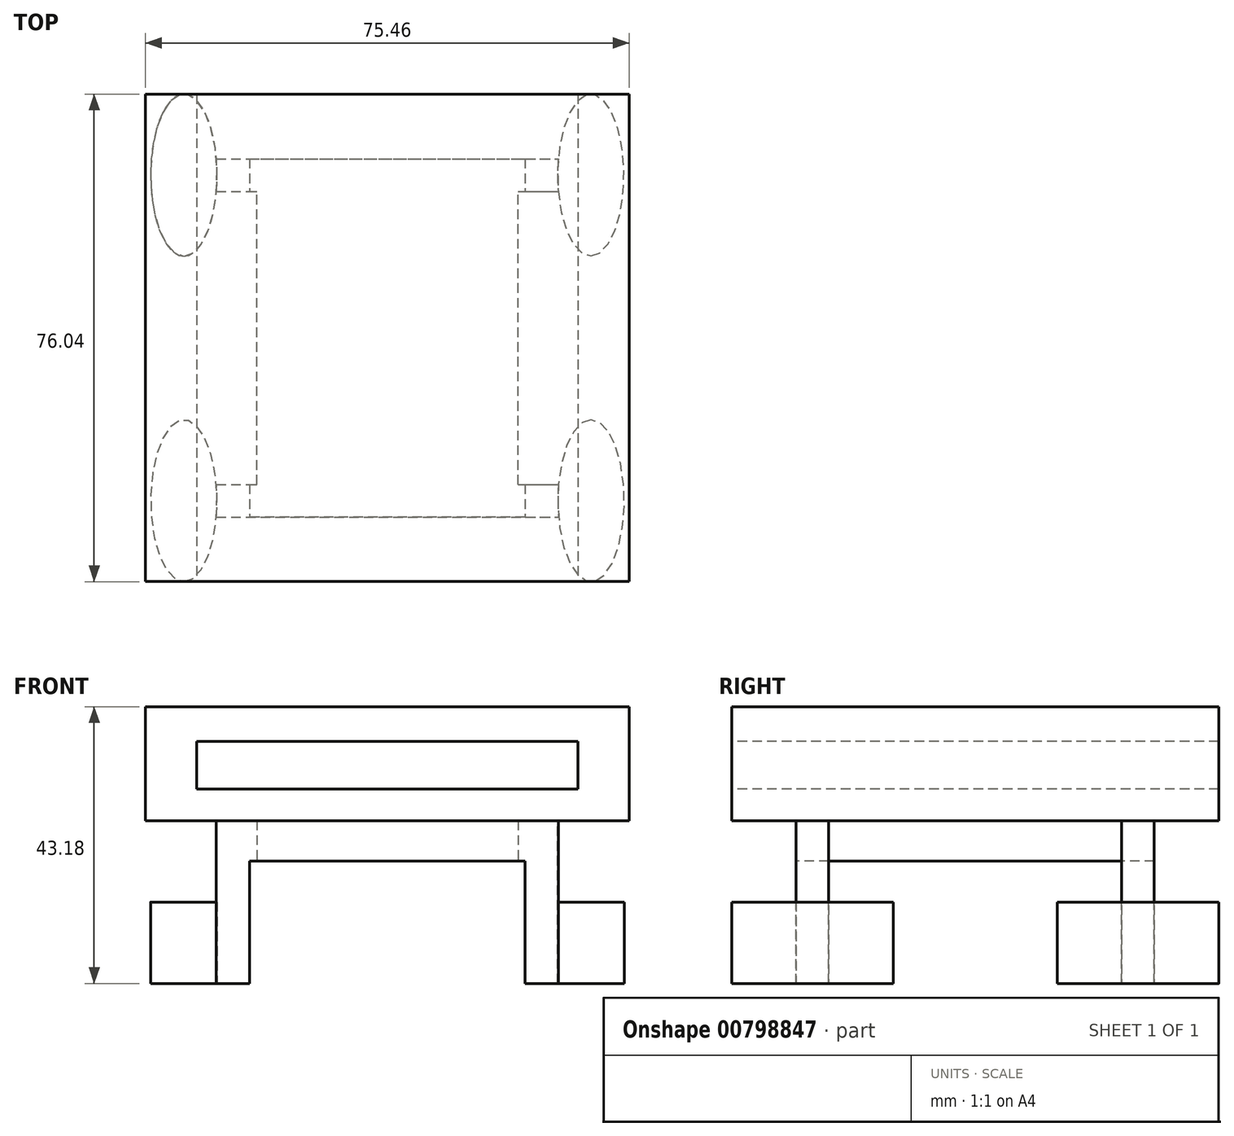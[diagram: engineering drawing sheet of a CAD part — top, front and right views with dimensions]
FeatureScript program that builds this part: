
annotation { "Feature Type Name" : "Feature", "Feature Type Description" : "" }
export const myFeature = defineFeature(function(context is Context, id is Id, definition is map)
    precondition{}
    {
        {
            var Q0;
            Q0=qCreatedBy(makeId("Top.planeOp"),FACE);
            var sketch = newSketch(context, id + "F0", { "sketchPlane" : qUnion([Q0])});
            skEllipse(sketch, "E0", {"center": v(-31.75, 25.4) * mm, "majorRadius": 12.62 * mm, "minorRadius": 5.19 * mm, "majorAxis": v(0, -1)});
            skEllipse(sketch, "E1.2.0", {"center": v(31.8, -25.4) * mm, "majorRadius": 12.62 * mm, "minorRadius": 5.19 * mm, "majorAxis": v(0, 1)});
            skPoint(sketch, "E1.center", {"position": v(0.02, 0) * mm});
            skEllipse(sketch, "E2", {"center": v(31.75, 25.4) * mm, "majorRadius": 12.6 * mm, "minorRadius": 5.18 * mm, "majorAxis": v(0, -1)});
            skEllipse(sketch, "E3", {"center": v(-31.75, -25.4) * mm, "majorRadius": 12.6 * mm, "minorRadius": 5.18 * mm, "majorAxis": v(0, -1)});
            skLineSegment(sketch, "E4", {"start": v(-26.67, 22.86) * mm, "end": v(-20.35, 22.86) * mm});
            skLineSegment(sketch, "E5.MirrorCS", {"start": v(-26.67, 27.94) * mm, "end": v(26.67, 27.94) * mm});
            skPoint(sketch, "E6.orphan", {"position": v(0, 0) * mm});
            skLineSegment(sketch, "E7.MirrorCS", {"start": v(-26.66, -22.86) * mm, "end": v(-20.35, -22.86) * mm});
            skLineSegment(sketch, "E8.MirrorCS", {"start": v(-26.67, -27.94) * mm, "end": v(26.67, -27.94) * mm});
            skPoint(sketch, "E9.start.orphan", {"position": v(-37.19, 0) * mm});
            skPoint(sketch, "E10.end.orphan", {"position": v(26.6, -25.4) * mm});
            skPoint(sketch, "E10.start.orphan", {"position": v(-26.57, -25.4) * mm});
            skLineSegment(sketch, "E11", {"start": v(26.68, -22.86) * mm, "end": v(26.71, -22.86) * mm});
            skLineSegment(sketch, "E12", {"start": v(26.67, -27.94) * mm, "end": v(26.71, -27.94) * mm});
            skLineSegment(sketch, "E13", {"start": v(-26.67, -27.94) * mm, "end": v(-26.67, -27.94) * mm});
            skLineSegment(sketch, "E14", {"start": v(-26.66, -22.86) * mm, "end": v(-26.67, -22.86) * mm});
            skLineSegment(sketch, "E15.left", {"start": v(20.4, -22.86) * mm, "end": v(20.4, 22.86) * mm});
            skLineSegment(sketch, "E15.right", {"start": v(-20.35, -22.86) * mm, "end": v(-20.35, 22.86) * mm});
            skLineSegment(sketch, "E16.trimOffspring", {"start": v(20.4, -22.86) * mm, "end": v(26.68, -22.86) * mm});
            skLineSegment(sketch, "E17.trimOffspring", {"start": v(20.4, 22.86) * mm, "end": v(26.67, 22.86) * mm});
            skSolve(sketch);
        }
        {
            var Q0;
            {var subQ0=sQuery(id+"F0.wireOp",EDGE,"E0");var subQ1=makeQuery(id+"F0.imprint","INTERSECT",VERTEX,{"derivedFrom":[subQ0,sQuery(id+"F0.wireOp",EDGE,"E4")]});Q0=makeQuery(id+"F0.imprint","IMPRINT",FACE,{"disambiguationData":[TD([[makeQuery(id+"F0.imprint","IMPRINT",EDGE,{"disambiguationData":[TD([[subQ1,-1.0]])],"derivedFrom":subQ0}),1.0]])]});}
            var Q1;
            {var subQ0=sQuery(id+"F0.wireOp",EDGE,"E1.2.0");var subQ1=makeQuery(id+"F0.imprint","INTERSECT",VERTEX,{"derivedFrom":[subQ0,sQuery(id+"F0.wireOp",EDGE,"E11")]});Q1=makeQuery(id+"F0.imprint","IMPRINT",FACE,{"disambiguationData":[TD([[makeQuery(id+"F0.imprint","IMPRINT",EDGE,{"disambiguationData":[TD([[subQ1,-1.0]])],"derivedFrom":subQ0}),1.0]])]});}
            var Q2;
            {var subQ0=sQuery(id+"F0.wireOp",EDGE,"E2");var subQ1=makeQuery(id+"F0.imprint","INTERSECT",VERTEX,{"derivedFrom":[subQ0,sQuery(id+"F0.wireOp",EDGE,"E5.MirrorCS")]});Q2=makeQuery(id+"F0.imprint","IMPRINT",FACE,{"disambiguationData":[TD([[makeQuery(id+"F0.imprint","IMPRINT",EDGE,{"disambiguationData":[TD([[subQ1,-1.0]])],"derivedFrom":subQ0}),1.0]])]});}
            var Q3;
            {var subQ0=sQuery(id+"F0.wireOp",EDGE,"E3");var subQ1=makeQuery(id+"F0.imprint","INTERSECT",VERTEX,{"derivedFrom":[subQ0,sQuery(id+"F0.wireOp",EDGE,"E13")]});Q3=makeQuery(id+"F0.imprint","IMPRINT",FACE,{"disambiguationData":[TD([[makeQuery(id+"F0.imprint","IMPRINT",EDGE,{"disambiguationData":[TD([[subQ1,-1.0]])],"derivedFrom":subQ0}),1.0]])]});}
            extrude(context, id + "F1", {"entities" : qUnion([Q0, Q1, Q2, Q3]), "depth" : 12.7 * mm, "offsetDistance" : 25.4 * mm});
        }
        {
            var Q0;
            {var subQ3=sQuery(id+"F0.wireOp",EDGE,"E4");Q0=makeQuery(id+"F0.imprint","IMPRINT",FACE,{"disambiguationData":[TD([[makeQuery(id+"F0.imprint","IMPRINT",EDGE,{"derivedFrom":subQ3}),1.0]])]});}
            extrude(context, id + "F2", {"entities" : qUnion([Q0]), "depth" : 25.4 * mm, "offsetDistance" : 25.4 * mm});
        }
        {
            var Q0;
            Q0=makeQuery(id+"F2.opExtrude","CAP_FACE",FACE,{"disambiguationData":[OSD([sQuery(id+"F0.wireOp",EDGE,"E0"),sQuery(id+"F0.wireOp",EDGE,"E1.2.0"),sQuery(id+"F0.wireOp",EDGE,"E2"),sQuery(id+"F0.wireOp",EDGE,"E3"),sQuery(id+"F0.wireOp",EDGE,"E4"),sQuery(id+"F0.wireOp",EDGE,"E5.MirrorCS"),sQuery(id+"F0.wireOp",EDGE,"E7.MirrorCS"),sQuery(id+"F0.wireOp",EDGE,"E8.MirrorCS"),sQuery(id+"F0.wireOp",EDGE,"E11"),sQuery(id+"F0.wireOp",EDGE,"E12"),sQuery(id+"F0.wireOp",EDGE,"E13"),sQuery(id+"F0.wireOp",EDGE,"E14"),sQuery(id+"F0.wireOp",EDGE,"E15.left"),sQuery(id+"F0.wireOp",EDGE,"E15.right"),sQuery(id+"F0.wireOp",EDGE,"E16.trimOffspring"),sQuery(id+"F0.wireOp",EDGE,"E17.trimOffspring")])],"isStart":false});
            var sketch = newSketch(context, id + "F3", { "sketchPlane" : qUnion([Q0])});
            skLineSegment(sketch, "E18.bottom", {"start": v(37.73, -38.02) * mm, "end": v(-37.73, -38.02) * mm});
            skLineSegment(sketch, "E18.top", {"start": v(37.73, 38.02) * mm, "end": v(-37.73, 38.02) * mm});
            skLineSegment(sketch, "E18.left", {"start": v(37.73, -38.02) * mm, "end": v(37.73, 38.02) * mm});
            skLineSegment(sketch, "E18.right", {"start": v(-37.73, -38.02) * mm, "end": v(-37.73, 38.02) * mm});
            skPoint(sketch, "E18.middle", {"position": v(0, 0) * mm});
            skPoint(sketch, "E18.cornerSnap0", {"position": v(31.8, -38.02) * mm});
            skSolve(sketch);
        }
        {
            var Q0;
            Q0 = qSketchRegion(id + "F3", true);
            extrude(context, id + "F4", {"entities" : qUnion([Q0]), "operationType" : NewBodyOperationType.ADD, "depth" : 5.08 * mm, "offsetDistance" : 25.4 * mm});
        }
        {
            var Q0;
            Q0=makeQuery(id+"F4.opExtrude","CAP_FACE",FACE,{"disambiguationData":[OSD([sQuery(id+"F3.wireOp",EDGE,"E18.bottom"),sQuery(id+"F3.wireOp",EDGE,"E18.top"),sQuery(id+"F3.wireOp",EDGE,"E18.left"),sQuery(id+"F3.wireOp",EDGE,"E18.right")])],"isStart":false});
            var sketch = newSketch(context, id + "F5", { "sketchPlane" : qUnion([Q0])});
            skLineSegment(sketch, "E19", {"start": v(-31.38, 31.67) * mm, "end": v(31.38, 31.67) * mm});
            skLineSegment(sketch, "E20", {"start": v(31.38, 31.67) * mm, "end": v(31.38, -31.67) * mm});
            skLineSegment(sketch, "E21", {"start": v(31.38, -31.67) * mm, "end": v(-31.38, -31.67) * mm});
            skLineSegment(sketch, "E22", {"start": v(-31.38, -31.67) * mm, "end": v(-31.38, 31.67) * mm});
            skSolve(sketch);
        }
        {
            var Q0;
            Q0=makeQuery(id+"F5.imprint","IMPRINT",FACE,{"disambiguationData":[TD([[makeQuery(id+"F5.imprint","IMPRINT",EDGE,{"derivedFrom":sQuery(id+"F5.wireOp",EDGE,"E19")}),1.0]])]});
            var Q1;
            Q1=makeQuery(id+"F5.imprint","IMPRINT",FACE,{"disambiguationData":[TD([[makeQuery(id+"F5.imprint","IMPRINT",EDGE,{"derivedFrom":sQuery(id+"F5.wireOp",EDGE,"E19")}),-1.0]])]});
            extrude(context, id + "F6", {"entities" : qUnion([Q0, Q1]), "operationType" : NewBodyOperationType.ADD, "depth" : 12.7 * mm, "offsetDistance" : 25.4 * mm});
        }
        {
            var Q0;
            {var subQ0=sQuery(id+"F3.wireOp",EDGE,"E18.bottom");Q0=makeQuery(id+"F6.boolean.opBoolean","MERGE",FACE,{"derivedFrom":[makeQuery(id+"F4.opExtrude","SWEPT_FACE",FACE,{"disambiguationData":[OSD([subQ0])]}),makeQuery(id+"F6.opExtrude","SWEPT_FACE",FACE,{"disambiguationData":[OSD([subQ0])]})]});}
            var sketch = newSketch(context, id + "F7", { "sketchPlane" : qUnion([Q0])});
            skLineSegment(sketch, "E23.bottom", {"start": v(29.75, 30.32) * mm, "end": v(-29.75, 30.32) * mm});
            skLineSegment(sketch, "E23.top", {"start": v(29.75, 37.73) * mm, "end": v(-29.75, 37.73) * mm});
            skLineSegment(sketch, "E23.left", {"start": v(29.75, 30.32) * mm, "end": v(29.75, 37.73) * mm});
            skLineSegment(sketch, "E23.right", {"start": v(-29.75, 30.32) * mm, "end": v(-29.75, 37.73) * mm});
            skPoint(sketch, "E23.middle", {"position": v(0, 34.03) * mm});
            skSolve(sketch);
        }
        {
            var Q0;
            Q0 = qSketchRegion(id + "F7", true);
            extrude(context, id + "F8", {"entities" : qUnion([Q0]), "operationType" : NewBodyOperationType.REMOVE, "oppositeDirection" : true, "depth" : 76.2 * mm, "offsetDistance" : 25.4 * mm});
        }
        {
            var Q0;
            Q0=makeQuery(id+"F2.opExtrude","SWEPT_FACE",FACE,{"disambiguationData":[OSD([sQuery(id+"F0.wireOp",EDGE,"E8.MirrorCS")])]});
            var sketch = newSketch(context, id + "F9", { "sketchPlane" : qUnion([Q0])});
            skLineSegment(sketch, "E24.bottom", {"start": v(21.5, 0) * mm, "end": v(-21.5, 0) * mm});
            skLineSegment(sketch, "E24.top", {"start": v(21.5, 19.08) * mm, "end": v(-21.5, 19.08) * mm});
            skLineSegment(sketch, "E24.left", {"start": v(21.5, 0) * mm, "end": v(21.5, 19.08) * mm});
            skLineSegment(sketch, "E24.right", {"start": v(-21.5, 0) * mm, "end": v(-21.5, 19.08) * mm});
            skPoint(sketch, "E24.middle", {"position": v(0, 9.54) * mm});
            skSolve(sketch);
        }
        {
            var Q0;
            Q0 = qSketchRegion(id + "F9", true);
            extrude(context, id + "F10", {"entities" : qUnion([Q0]), "operationType" : NewBodyOperationType.REMOVE, "oppositeDirection" : true, "depth" : 76.2 * mm, "offsetDistance" : 25.4 * mm});
        }
    });
